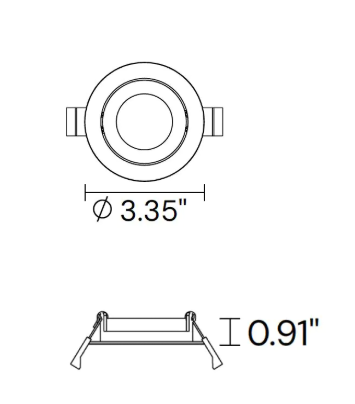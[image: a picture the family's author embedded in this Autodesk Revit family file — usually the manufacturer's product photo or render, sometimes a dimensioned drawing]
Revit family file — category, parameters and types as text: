
# Revit family: Alcon-14078-ADJ-6-Revit-Family
name_source: partatom
category: Lighting Fixtures
units: mm (PartAtom-declared; Revit-internal decimal feet)

## family parameters
Always vertical = Yes
Cut with Voids When Loaded = No
Host = Ceiling
Light Source = Yes
OmniClass Number = 23.80.70.11
OmniClass Title = Luminaries for Internal Lighting
Part Type = Normal
Room Calculation Point = No
Round Connector Dimension = Use Diameter
Shared = No

## types (1)
- Type 1
    Color Filter = 16777215
    Default Elevation = 0' - 0"
    Dimming Lamp Color Temperature Shift = <None>
    Housing = Default
    Lens = Default
    Light Source Symbol Length = 10' - 0"
    LightSource = light
    Link To Product Page = https://www.alconlighting.com
    Manufacturer = Alcon Light
    Product Identity = Alcon Lighting 14078-ADJ-6
    Reflector = Default metal
    Spot Beam Angle = 30.00°
    Spot Field Angle = 90.00°
    Tilt Angle = 60.00°

## geometry (parser evidence)
native form markers: Sweep x2
no freeform markers — native parametric forms only
